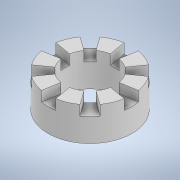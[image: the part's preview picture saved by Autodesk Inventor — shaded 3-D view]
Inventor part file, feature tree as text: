
AUTODESK INVENTOR PART (.ipt)
format: ipt  version: 2021.1 (Build 251245010, 245A)  size: 146,432 bytes
history: native  units: mm
features: extrude x2, sketch x2, other x1
ambient origin geometry x8: Origin, YZ Plane, XZ Plane, XY Plane, X Axis, Y Axis, Z Axis, Center Point
bodies: Body1 (feature_tree)
feature tree (5):
  other  "Твердое тело1"
  extrude  "Выдавливание1"  Depth=25.0mm
  extrude  "Выдавливание2"  Depth=15.0mm
  sketch  "Эскиз1"
  sketch  "Эскиз2"
